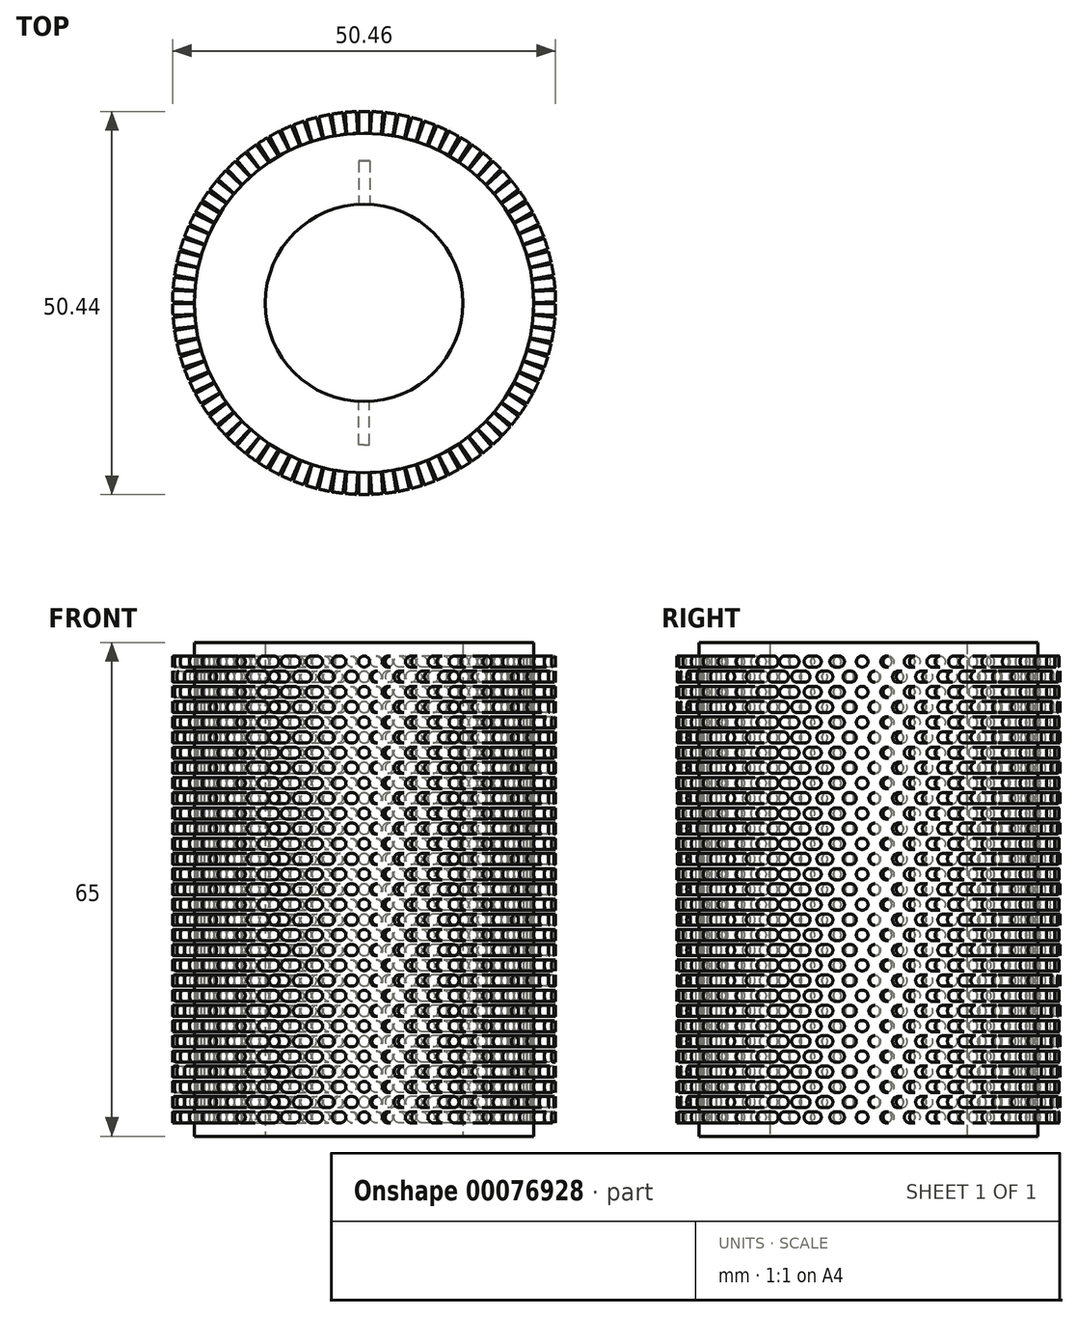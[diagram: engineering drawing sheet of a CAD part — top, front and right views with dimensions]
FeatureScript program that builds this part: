
annotation { "Feature Type Name" : "Feature", "Feature Type Description" : "" }
export const myFeature = defineFeature(function(context is Context, id is Id, definition is map)
    precondition{}
    {
        {
            var Q0;
            Q0=qCreatedBy(makeId("Top.planeOp"),FACE);
            var sketch = newSketch(context, id + "F0", { "sketchPlane" : qUnion([Q0])});
            skCircle(sketch, "E0", {"center": v(0, 0) * mm, "radius": 18.71 * mm});
            skCircle(sketch, "E1", {"center": v(0, 0) * mm, "radius": 13 * mm});
            skSolve(sketch);
        }
        {
            var Q0;
            Q0=makeQuery(id+"F0.imprint","IMPRINT",FACE,{"disambiguationData":[TD([[makeQuery(id+"F0.imprint","IMPRINT",EDGE,{"derivedFrom":sQuery(id+"F0.wireOp",EDGE,"E0")}),1.0]])]});
            extrude(context, id + "F1", {"entities" : qUnion([Q0]), "depth" : 32.5 * mm, "hasSecondDirection" : true, "secondDirectionOppositeDirection" : true, "secondDirectionDepth" : 32.5 * mm});
        }
        {
            var Q0;
            Q0=qCreatedBy(makeId("Top.planeOp"),FACE);
            var sketch = newSketch(context, id + "F2", { "sketchPlane" : qUnion([Q0])});
            skCircle(sketch, "E2", {"center": v(0, 0) * mm, "radius": 22.35 * mm});
            skCircle(sketch, "E3.0", {"center": v(0, 0) * mm, "radius": 18.71 * mm});
            skSolve(sketch);
        }
        {
            var Q0;
            Q0=makeQuery(id+"F2.imprint","IMPRINT",FACE,{"disambiguationData":[TD([[makeQuery(id+"F2.imprint","IMPRINT",EDGE,{"derivedFrom":sQuery(id+"F2.wireOp",EDGE,"E2")}),1.0]])]});
            var Q1;
            Q1=makeQuery(id+"F1.opExtrude","CAP_FACE",FACE,{"disambiguationData":[OSD([sQuery(id+"F0.wireOp",EDGE,"E0"),sQuery(id+"F0.wireOp",EDGE,"E1")])],"isStart":false});
            extrude(context, id + "F3", {"entities" : qUnion([Q0]), "endBound" : BoundingType.SYMMETRIC, "endBoundEntityFace" : qUnion([Q1]), "depth" : 65 * mm});
        }
        {
            var Q0;
            Q0=qCreatedBy(makeId("Front.planeOp"),FACE);
            var sketch = newSketch(context, id + "F4", { "sketchPlane" : qUnion([Q0])});
            skCircle(sketch, "E4", {"center": v(0, 0) * mm, "radius": 0.73 * mm});
            skCircle(sketch, "E5.0.1.0", {"center": v(0, 4) * mm, "radius": 0.73 * mm});
            skCircle(sketch, "E5.0.2.0", {"center": v(0, 8) * mm, "radius": 0.73 * mm});
            skCircle(sketch, "E5.0.3.0", {"center": v(0, 12) * mm, "radius": 0.73 * mm});
            skCircle(sketch, "E5.0.4.0", {"center": v(0, 16) * mm, "radius": 0.73 * mm});
            skCircle(sketch, "E5.0.5.0", {"center": v(0, 20) * mm, "radius": 0.73 * mm});
            skCircle(sketch, "E5.0.6.0", {"center": v(0, 24) * mm, "radius": 0.73 * mm});
            skLineSegment(sketch, "E5.direction1", {"start": v(0, 0) * mm, "end": v(15.56, 0) * mm, "construction": true});
            skLineSegment(sketch, "E5.direction2", {"start": v(0, 0) * mm, "end": v(0, 4) * mm, "construction": true});
            skCircle(sketch, "E6.0.1.0", {"center": v(0, -4) * mm, "radius": 0.73 * mm});
            skCircle(sketch, "E6.0.2.0", {"center": v(0, -8) * mm, "radius": 0.73 * mm});
            skCircle(sketch, "E6.0.3.0", {"center": v(0, -12) * mm, "radius": 0.73 * mm});
            skCircle(sketch, "E6.0.4.0", {"center": v(0, -16) * mm, "radius": 0.73 * mm});
            skCircle(sketch, "E6.0.5.0", {"center": v(0, -20) * mm, "radius": 0.73 * mm});
            skCircle(sketch, "E6.0.6.0", {"center": v(0, -24) * mm, "radius": 0.73 * mm});
            skLineSegment(sketch, "E6.direction1", {"start": v(0, 0) * mm, "end": v(25, 0) * mm, "construction": true});
            skLineSegment(sketch, "E6.direction2", {"start": v(0, 0) * mm, "end": v(0, -4) * mm, "construction": true});
            skCircle(sketch, "E7.0.0.7", {"center": v(0, 28) * mm, "radius": 0.73 * mm});
            skCircle(sketch, "E8.0.0.7", {"center": v(0, -28) * mm, "radius": 0.73 * mm});
            skSolve(sketch);
        }
        {
            var Q0;
            Q0 = qSketchRegion(id + "F4", true);
            extrude(context, id + "F5", {"entities" : qUnion([Q0]), "operationType" : NewBodyOperationType.REMOVE, "endBound" : BoundingType.THROUGH_ALL, "oppositeDirection" : true, "depth" : 25 * mm});
        }
        {
            var Q0;
            Q0=qCreatedBy(makeId("Front.planeOp"),FACE);
            var sketch = newSketch(context, id + "F6", { "sketchPlane" : qUnion([Q0])});
            skCircle(sketch, "E9", {"center": v(0, 2) * mm, "radius": 0.72 * mm});
            skLineSegment(sketch, "E10", {"start": v(-13.56, 0) * mm, "end": v(16.56, 0) * mm, "construction": true});
            skCircle(sketch, "E11.0.1.0", {"center": v(0, 6) * mm, "radius": 0.72 * mm});
            skCircle(sketch, "E11.0.2.0", {"center": v(0, 10) * mm, "radius": 0.72 * mm});
            skCircle(sketch, "E11.0.3.0", {"center": v(0, 14) * mm, "radius": 0.72 * mm});
            skCircle(sketch, "E11.0.4.0", {"center": v(0, 18) * mm, "radius": 0.72 * mm});
            skCircle(sketch, "E11.0.5.0", {"center": v(0, 22) * mm, "radius": 0.72 * mm});
            skCircle(sketch, "E11.0.6.0", {"center": v(0, 26) * mm, "radius": 0.72 * mm});
            skCircle(sketch, "E11.0.7.0", {"center": v(0, 30) * mm, "radius": 0.72 * mm});
            skLineSegment(sketch, "E11.direction1", {"start": v(0, 2) * mm, "end": v(25, 2) * mm, "construction": true});
            skLineSegment(sketch, "E11.direction2", {"start": v(0, 2) * mm, "end": v(0, 6) * mm, "construction": true});
            skCircle(sketch, "E12.MirrorC", {"center": v(0, -14) * mm, "radius": 0.72 * mm});
            skCircle(sketch, "E13.MirrorC", {"center": v(0, -10) * mm, "radius": 0.72 * mm});
            skCircle(sketch, "E14.MirrorC", {"center": v(0, -26) * mm, "radius": 0.72 * mm});
            skCircle(sketch, "E15.MirrorC", {"center": v(0, -22) * mm, "radius": 0.72 * mm});
            skCircle(sketch, "E16.MirrorC", {"center": v(0, -18) * mm, "radius": 0.72 * mm});
            skCircle(sketch, "E17.MirrorC", {"center": v(0, -6) * mm, "radius": 0.72 * mm});
            skCircle(sketch, "E18.MirrorC", {"center": v(0, -2) * mm, "radius": 0.72 * mm});
            skCircle(sketch, "E19.MirrorC", {"center": v(0, -30) * mm, "radius": 0.72 * mm});
            skSolve(sketch);
        }
        {
            var Q0;
            Q0 = qSketchRegion(id + "F6", true);
            extrude(context, id + "F7", {"entities" : qUnion([Q0]), "operationType" : NewBodyOperationType.REMOVE, "endBound" : BoundingType.THROUGH_ALL, "depth" : 25 * mm});
        }
        {
            var Q0;
            Q0=qCreatedBy(makeId("Front.planeOp"),FACE);
            var sketch = newSketch(context, id + "F8", { "sketchPlane" : qUnion([Q0])});
            skLineSegment(sketch, "E20", {"start": v(0, 65.95) * mm, "end": v(0, -70.4) * mm, "construction": true});
            skSolve(sketch);
        }
        {
            var Q0;
            Q0=qCreatedBy(makeId("Front.planeOp"),FACE);
            cPlane(context, id + "F9", {"entities" : qUnion([Q0]), "cplaneType" : CPlaneType.OFFSET, "offset" : 37.43 * mm / 2, "oppositeDirection" : true, "width" : 150 * mm, "height" : 150 * mm});
        }
        {
            var Q0;
            Q0=qCreatedBy(id+"F9.planeOp",FACE);
            var sketch = newSketch(context, id + "F10", { "sketchPlane" : qUnion([Q0])});
            skCircle(sketch, "E21.0", {"center": v(0, -28) * mm, "radius": 0.73 * mm});
            skCircle(sketch, "E22.0", {"center": v(0, -24) * mm, "radius": 0.73 * mm});
            skCircle(sketch, "E23.0", {"center": v(0, -20) * mm, "radius": 0.73 * mm});
            skCircle(sketch, "E24.0", {"center": v(0, -16) * mm, "radius": 0.73 * mm});
            skCircle(sketch, "E25.0", {"center": v(0, -12) * mm, "radius": 0.73 * mm});
            skCircle(sketch, "E26.0", {"center": v(0, -8) * mm, "radius": 0.73 * mm});
            skCircle(sketch, "E27.0", {"center": v(0, -4) * mm, "radius": 0.73 * mm});
            skCircle(sketch, "E28.0", {"center": v(0, 0) * mm, "radius": 0.73 * mm});
            skCircle(sketch, "E29.0", {"center": v(0, 4) * mm, "radius": 0.73 * mm});
            skCircle(sketch, "E30.0", {"center": v(0, 8) * mm, "radius": 0.73 * mm});
            skCircle(sketch, "E31.0", {"center": v(0, 12) * mm, "radius": 0.73 * mm});
            skCircle(sketch, "E32.0", {"center": v(0, 16) * mm, "radius": 0.73 * mm});
            skCircle(sketch, "E33.0", {"center": v(0, 20) * mm, "radius": 0.73 * mm});
            skCircle(sketch, "E34.0", {"center": v(0, 24) * mm, "radius": 0.73 * mm});
            skCircle(sketch, "E35.0", {"center": v(0, 28) * mm, "radius": 0.73 * mm});
            skSolve(sketch);
        }
        {
            var Q0;
            Q0 = qSketchRegion(id + "F10", true);
            extrude(context, id + "F11", {"entities" : qUnion([Q0]), "oppositeDirection" : true, "depth" : 6.5 * mm});
        }
        {
            var Q0;
            Q0=makeQuery(id+"F11.opExtrude","SWEPT_BODY",BODY,{"disambiguationData":[OSD([sQuery(id+"F10.wireOp",EDGE,"E21.0")])]});
            var Q1;
            Q1=makeQuery(id+"F11.opExtrude","SWEPT_BODY",BODY,{"disambiguationData":[OSD([sQuery(id+"F10.wireOp",EDGE,"E22.0")])]});
            var Q2;
            Q2=makeQuery(id+"F11.opExtrude","SWEPT_BODY",BODY,{"disambiguationData":[OSD([sQuery(id+"F10.wireOp",EDGE,"E23.0")])]});
            var Q3;
            Q3=makeQuery(id+"F11.opExtrude","SWEPT_BODY",BODY,{"disambiguationData":[OSD([sQuery(id+"F10.wireOp",EDGE,"E24.0")])]});
            var Q4;
            Q4=makeQuery(id+"F11.opExtrude","SWEPT_BODY",BODY,{"disambiguationData":[OSD([sQuery(id+"F10.wireOp",EDGE,"E25.0")])]});
            var Q5;
            Q5=makeQuery(id+"F11.opExtrude","SWEPT_BODY",BODY,{"disambiguationData":[OSD([sQuery(id+"F10.wireOp",EDGE,"E26.0")])]});
            var Q6;
            Q6=makeQuery(id+"F11.opExtrude","SWEPT_BODY",BODY,{"disambiguationData":[OSD([sQuery(id+"F10.wireOp",EDGE,"E27.0")])]});
            var Q7;
            Q7=makeQuery(id+"F11.opExtrude","SWEPT_BODY",BODY,{"disambiguationData":[OSD([sQuery(id+"F10.wireOp",EDGE,"E28.0")])]});
            var Q8;
            Q8=makeQuery(id+"F11.opExtrude","SWEPT_BODY",BODY,{"disambiguationData":[OSD([sQuery(id+"F10.wireOp",EDGE,"E29.0")])]});
            var Q9;
            Q9=makeQuery(id+"F11.opExtrude","SWEPT_BODY",BODY,{"disambiguationData":[OSD([sQuery(id+"F10.wireOp",EDGE,"E30.0")])]});
            var Q10;
            Q10=makeQuery(id+"F11.opExtrude","SWEPT_BODY",BODY,{"disambiguationData":[OSD([sQuery(id+"F10.wireOp",EDGE,"E31.0")])]});
            var Q11;
            Q11=makeQuery(id+"F11.opExtrude","SWEPT_BODY",BODY,{"disambiguationData":[OSD([sQuery(id+"F10.wireOp",EDGE,"E32.0")])]});
            var Q12;
            Q12=makeQuery(id+"F11.opExtrude","SWEPT_BODY",BODY,{"disambiguationData":[OSD([sQuery(id+"F10.wireOp",EDGE,"E33.0")])]});
            var Q13;
            Q13=makeQuery(id+"F11.opExtrude","SWEPT_BODY",BODY,{"disambiguationData":[OSD([sQuery(id+"F10.wireOp",EDGE,"E34.0")])]});
            var Q14;
            Q14=makeQuery(id+"F11.opExtrude","SWEPT_BODY",BODY,{"disambiguationData":[OSD([sQuery(id+"F10.wireOp",EDGE,"E35.0")])]});
            var Q15;
            Q15=sQuery(id+"F8.wireOp",EDGE,"E20");
            circularPattern(context, id + "F12", {"operationType" : NewBodyOperationType.ADD, "entities" : qUnion([Q0, Q1, Q2, Q3, Q4, Q5, Q6, Q7, Q8, Q9, Q10, Q11, Q12, Q13, Q14]), "axis" : qUnion([Q15]), "angle" : 8 * degree, "instanceCount" : 45});
        }
        {
            var Q0;
            Q0=qCreatedBy(makeId("Front.planeOp"),FACE);
            cPlane(context, id + "F13", {"entities" : qUnion([Q0]), "cplaneType" : CPlaneType.OFFSET, "offset" : 18.71 * mm, "width" : 150 * mm, "height" : 150 * mm});
        }
        {
            var Q0;
            Q0=qCreatedBy(id+"F13.planeOp",FACE);
            var sketch = newSketch(context, id + "F14", { "sketchPlane" : qUnion([Q0])});
            skCircle(sketch, "E36.0", {"center": v(0, 30) * mm, "radius": 0.72 * mm});
            skCircle(sketch, "E37.0", {"center": v(0, 26) * mm, "radius": 0.72 * mm});
            skCircle(sketch, "E38.0", {"center": v(0, 22) * mm, "radius": 0.72 * mm});
            skCircle(sketch, "E39.0", {"center": v(0, 18) * mm, "radius": 0.72 * mm});
            skCircle(sketch, "E40.0", {"center": v(0, 14) * mm, "radius": 0.72 * mm});
            skCircle(sketch, "E41.0", {"center": v(0, 10) * mm, "radius": 0.72 * mm});
            skCircle(sketch, "E42.0", {"center": v(0, 6) * mm, "radius": 0.72 * mm});
            skCircle(sketch, "E43.0", {"center": v(0, 2) * mm, "radius": 0.72 * mm});
            skCircle(sketch, "E44.0", {"center": v(0, -30) * mm, "radius": 0.72 * mm});
            skCircle(sketch, "E45.0", {"center": v(0, -26) * mm, "radius": 0.72 * mm});
            skCircle(sketch, "E46.0", {"center": v(0, -22) * mm, "radius": 0.72 * mm});
            skCircle(sketch, "E47.0", {"center": v(0, -18) * mm, "radius": 0.72 * mm});
            skCircle(sketch, "E48.0", {"center": v(0, -14) * mm, "radius": 0.72 * mm});
            skCircle(sketch, "E49.0", {"center": v(0, -10) * mm, "radius": 0.72 * mm});
            skCircle(sketch, "E50.0", {"center": v(0, -6) * mm, "radius": 0.72 * mm});
            skCircle(sketch, "E51.0", {"center": v(0, -2) * mm, "radius": 0.72 * mm});
            skSolve(sketch);
        }
        {
            var Q0;
            Q0 = qSketchRegion(id + "F14", true);
            extrude(context, id + "F15", {"entities" : qUnion([Q0]), "depth" : 6.5 * mm});
        }
        {
            var Q0;
            Q0=makeQuery(id+"F15.opExtrude","SWEPT_BODY",BODY,{"disambiguationData":[OSD([sQuery(id+"F14.wireOp",EDGE,"E44.0")])]});
            var Q1;
            Q1=makeQuery(id+"F15.opExtrude","SWEPT_BODY",BODY,{"disambiguationData":[OSD([sQuery(id+"F14.wireOp",EDGE,"E45.0")])]});
            var Q2;
            Q2=makeQuery(id+"F15.opExtrude","SWEPT_BODY",BODY,{"disambiguationData":[OSD([sQuery(id+"F14.wireOp",EDGE,"E46.0")])]});
            var Q3;
            Q3=makeQuery(id+"F15.opExtrude","SWEPT_BODY",BODY,{"disambiguationData":[OSD([sQuery(id+"F14.wireOp",EDGE,"E47.0")])]});
            var Q4;
            Q4=makeQuery(id+"F15.opExtrude","SWEPT_BODY",BODY,{"disambiguationData":[OSD([sQuery(id+"F14.wireOp",EDGE,"E48.0")])]});
            var Q5;
            Q5=makeQuery(id+"F15.opExtrude","SWEPT_BODY",BODY,{"disambiguationData":[OSD([sQuery(id+"F14.wireOp",EDGE,"E49.0")])]});
            var Q6;
            Q6=makeQuery(id+"F15.opExtrude","SWEPT_BODY",BODY,{"disambiguationData":[OSD([sQuery(id+"F14.wireOp",EDGE,"E50.0")])]});
            var Q7;
            Q7=makeQuery(id+"F15.opExtrude","SWEPT_BODY",BODY,{"disambiguationData":[OSD([sQuery(id+"F14.wireOp",EDGE,"E51.0")])]});
            var Q8;
            Q8=makeQuery(id+"F15.opExtrude","SWEPT_BODY",BODY,{"disambiguationData":[OSD([sQuery(id+"F14.wireOp",EDGE,"E43.0")])]});
            var Q9;
            Q9=makeQuery(id+"F15.opExtrude","SWEPT_BODY",BODY,{"disambiguationData":[OSD([sQuery(id+"F14.wireOp",EDGE,"E42.0")])]});
            var Q10;
            Q10=makeQuery(id+"F15.opExtrude","SWEPT_BODY",BODY,{"disambiguationData":[OSD([sQuery(id+"F14.wireOp",EDGE,"E41.0")])]});
            var Q11;
            Q11=makeQuery(id+"F15.opExtrude","SWEPT_BODY",BODY,{"disambiguationData":[OSD([sQuery(id+"F14.wireOp",EDGE,"E40.0")])]});
            var Q12;
            Q12=makeQuery(id+"F15.opExtrude","SWEPT_BODY",BODY,{"disambiguationData":[OSD([sQuery(id+"F14.wireOp",EDGE,"E39.0")])]});
            var Q13;
            Q13=makeQuery(id+"F15.opExtrude","SWEPT_BODY",BODY,{"disambiguationData":[OSD([sQuery(id+"F14.wireOp",EDGE,"E38.0")])]});
            var Q14;
            Q14=makeQuery(id+"F15.opExtrude","SWEPT_BODY",BODY,{"disambiguationData":[OSD([sQuery(id+"F14.wireOp",EDGE,"E37.0")])]});
            var Q15;
            Q15=makeQuery(id+"F15.opExtrude","SWEPT_BODY",BODY,{"disambiguationData":[OSD([sQuery(id+"F14.wireOp",EDGE,"E36.0")])]});
            var Q16;
            Q16=sQuery(id+"F8.wireOp",EDGE,"E20");
            circularPattern(context, id + "F16", {"operationType" : NewBodyOperationType.ADD, "entities" : qUnion([Q0, Q1, Q2, Q3, Q4, Q5, Q6, Q7, Q8, Q9, Q10, Q11, Q12, Q13, Q14, Q15]), "axis" : qUnion([Q16]), "angle" : 8 * degree, "instanceCount" : 45});
        }
    });
